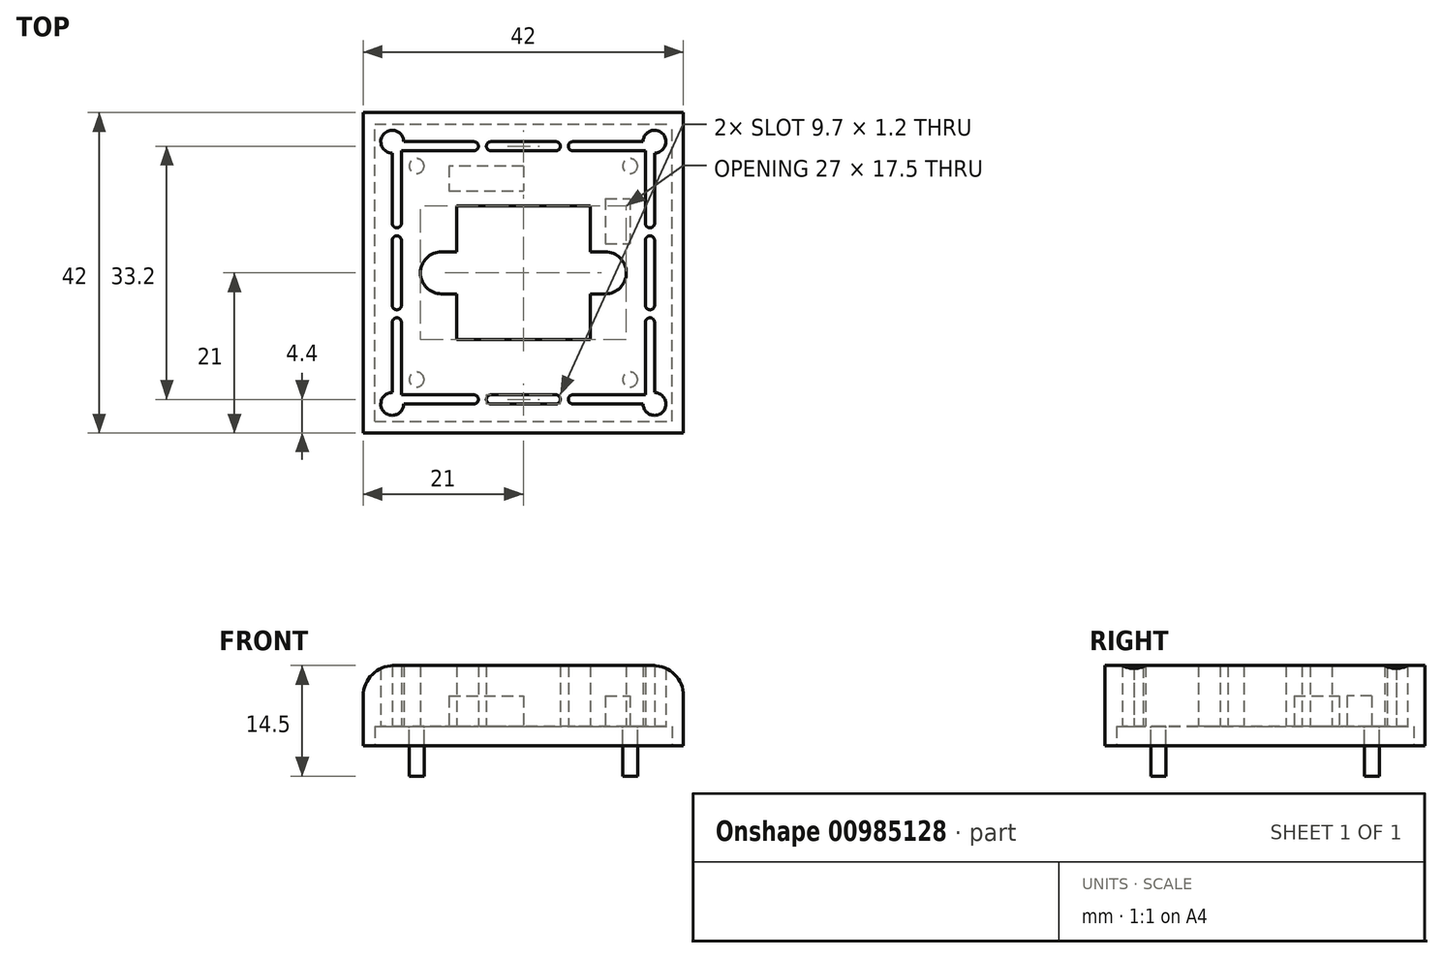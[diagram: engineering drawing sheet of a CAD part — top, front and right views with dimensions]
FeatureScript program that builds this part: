
annotation { "Feature Type Name" : "Feature", "Feature Type Description" : "" }
export const myFeature = defineFeature(function(context is Context, id is Id, definition is map)
    precondition{}
    {
        {
            var Q0;
            Q0=qCreatedBy(makeId("Top.planeOp"),FACE);
            var sketch = newSketch(context, id + "F0", { "sketchPlane" : qUnion([Q0])});
            skLineSegment(sketch, "E0.bottom", {"start": v(19, 19) * mm, "end": v(-19, 19) * mm, "construction": true});
            skLineSegment(sketch, "E0.top", {"start": v(19, -19) * mm, "end": v(-19, -19) * mm, "construction": true});
            skLineSegment(sketch, "E0.left", {"start": v(19, 19) * mm, "end": v(19, -19) * mm, "construction": true});
            skLineSegment(sketch, "E0.right", {"start": v(-19, 19) * mm, "end": v(-19, -19) * mm, "construction": true});
            skPoint(sketch, "E0.middle", {"position": v(0, 0) * mm});
            skPoint(sketch, "E1", {"position": v(19, 0) * mm});
            skPoint(sketch, "E2", {"position": v(-19, 0) * mm});
            skPoint(sketch, "E3", {"position": v(0, 19) * mm});
            skPoint(sketch, "E4", {"position": v(0, -19) * mm});
            skPoint(sketch, "E5", {"position": v(17.2, 0) * mm});
            skPoint(sketch, "E6", {"position": v(-17.2, 0) * mm});
            skLineSegment(sketch, "E7", {"start": v(-19, 0) * mm, "end": v(-17.2, 0) * mm, "construction": true});
            skLineSegment(sketch, "E8", {"start": v(19, 0) * mm, "end": v(17.2, 0) * mm, "construction": true});
            skLineSegment(sketch, "E9", {"start": v(0, 19) * mm, "end": v(0, 17.2) * mm, "construction": true});
            skLineSegment(sketch, "E10", {"start": v(0, -17.2) * mm, "end": v(0, -19) * mm, "construction": true});
            skPoint(sketch, "E11", {"position": v(-16, 16) * mm});
            skPoint(sketch, "E12", {"position": v(16, -16) * mm});
            skPoint(sketch, "E13", {"position": v(16, 16) * mm});
            skPoint(sketch, "E14", {"position": v(-16, -16) * mm});
            skPoint(sketch, "E15", {"position": v(17.2, 4.25) * mm});
            skPoint(sketch, "E16", {"position": v(17.2, -4.25) * mm});
            skPoint(sketch, "E17", {"position": v(16, -4.25) * mm});
            skPoint(sketch, "E18", {"position": v(16, 4.25) * mm});
            skPoint(sketch, "E19", {"position": v(-17.2, 4.25) * mm});
            skPoint(sketch, "E20", {"position": v(-16, 4.25) * mm});
            skPoint(sketch, "E21", {"position": v(-17.2, -4.25) * mm});
            skPoint(sketch, "E22", {"position": v(-16, -4.25) * mm});
            skPoint(sketch, "E23", {"position": v(-4.25, 17.2) * mm});
            skPoint(sketch, "E24", {"position": v(-4.25, 16) * mm});
            skPoint(sketch, "E25", {"position": v(4.25, 17.2) * mm});
            skPoint(sketch, "E26", {"position": v(4.25, 16) * mm});
            skPoint(sketch, "E27", {"position": v(-4.25, -16) * mm});
            skPoint(sketch, "E28", {"position": v(4.25, -16) * mm});
            skPoint(sketch, "E29", {"position": v(-4.25, -17.2) * mm});
            skPoint(sketch, "E30", {"position": v(4.25, -17.2) * mm});
            skLineSegment(sketch, "E31", {"start": v(17.2, 4.25) * mm, "end": v(17.2, -4.25) * mm});
            skLineSegment(sketch, "E32", {"start": v(16, 4.25) * mm, "end": v(16, -4.25) * mm});
            skLineSegment(sketch, "E33", {"start": v(4.25, 16) * mm, "end": v(-4.25, 16) * mm});
            skLineSegment(sketch, "E34", {"start": v(-4.25, 17.2) * mm, "end": v(4.25, 17.2) * mm});
            skLineSegment(sketch, "E35", {"start": v(-16, 4.25) * mm, "end": v(-16, -4.25) * mm});
            skLineSegment(sketch, "E36", {"start": v(-17.2, -4.25) * mm, "end": v(-17.2, 4.25) * mm});
            skLineSegment(sketch, "E37", {"start": v(-4.25, -16) * mm, "end": v(4.25, -16) * mm});
            skLineSegment(sketch, "E38", {"start": v(4.25, -17.2) * mm, "end": v(-4.25, -17.2) * mm});
            skArc(sketch, "E39", {"start": v(16, 4.25) * mm, "mid": v(16.6, 4.85) * mm, "end": v(17.2, 4.25) * mm});
            skArc(sketch, "E40", {"start": v(17.2, -4.25) * mm, "mid": v(16.6, -4.85) * mm, "end": v(16, -4.25) * mm});
            skArc(sketch, "E41", {"start": v(4.25, -16) * mm, "mid": v(4.85, -16.6) * mm, "end": v(4.25, -17.2) * mm});
            skArc(sketch, "E42", {"start": v(-4.25, -16) * mm, "mid": v(-4.85, -16.6) * mm, "end": v(-4.25, -17.2) * mm});
            skArc(sketch, "E43", {"start": v(-17.2, -4.25) * mm, "mid": v(-16.6, -4.85) * mm, "end": v(-16, -4.25) * mm});
            skArc(sketch, "E44", {"start": v(-17.2, 4.25) * mm, "mid": v(-16.6, 4.85) * mm, "end": v(-16, 4.25) * mm});
            skArc(sketch, "E45", {"start": v(-4.25, 16) * mm, "mid": v(-4.85, 16.6) * mm, "end": v(-4.25, 17.2) * mm});
            skArc(sketch, "E46", {"start": v(4.25, 16) * mm, "mid": v(4.85, 16.6) * mm, "end": v(4.25, 17.2) * mm});
            skPoint(sketch, "E47", {"position": v(-6.5, 16) * mm});
            skPoint(sketch, "E48", {"position": v(-6.5, 17.2) * mm});
            skPoint(sketch, "E49", {"position": v(-16, 6.5) * mm});
            skPoint(sketch, "E50", {"position": v(-17.2, 6.5) * mm});
            skPoint(sketch, "E51", {"position": v(6.5, 16) * mm});
            skPoint(sketch, "E52", {"position": v(6.5, 17.2) * mm});
            skPoint(sketch, "E53", {"position": v(16, 6.5) * mm});
            skPoint(sketch, "E54", {"position": v(17.2, 6.5) * mm});
            skPoint(sketch, "E55", {"position": v(-17.2, -6.5) * mm});
            skPoint(sketch, "E56", {"position": v(-16, -6.5) * mm});
            skPoint(sketch, "E57", {"position": v(17.2, -6.5) * mm});
            skPoint(sketch, "E58", {"position": v(16, -6.5) * mm});
            skPoint(sketch, "E59", {"position": v(6.5, -17.2) * mm});
            skPoint(sketch, "E60", {"position": v(6.5, -16) * mm});
            skPoint(sketch, "E61", {"position": v(-6.5, -17.2) * mm});
            skPoint(sketch, "E62", {"position": v(-6.5, -16) * mm});
            skLineSegment(sketch, "E63", {"start": v(-6.5, 17.2) * mm, "end": v(-6.5, 16) * mm, "construction": true});
            skLineSegment(sketch, "E64", {"start": v(-17.2, 6.5) * mm, "end": v(-16, 6.5) * mm, "construction": true});
            skLineSegment(sketch, "E65", {"start": v(6.5, 17.2) * mm, "end": v(6.5, 16) * mm, "construction": true});
            skLineSegment(sketch, "E66", {"start": v(16, 6.5) * mm, "end": v(17.2, 6.5) * mm, "construction": true});
            skLineSegment(sketch, "E67", {"start": v(-17.2, -6.5) * mm, "end": v(-16, -6.5) * mm, "construction": true});
            skLineSegment(sketch, "E68", {"start": v(-6.5, -16) * mm, "end": v(-6.5, -17.2) * mm, "construction": true});
            skLineSegment(sketch, "E69", {"start": v(16, -6.5) * mm, "end": v(17.2, -6.5) * mm, "construction": true});
            skLineSegment(sketch, "E70", {"start": v(6.5, -16) * mm, "end": v(6.5, -17.2) * mm, "construction": true});
            skArc(sketch, "E71", {"start": v(-6.5, 17.2) * mm, "mid": v(-5.9, 16.6) * mm, "end": v(-6.5, 16) * mm});
            skArc(sketch, "E72", {"start": v(-16, 6.5) * mm, "mid": v(-16.6, 5.9) * mm, "end": v(-17.2, 6.5) * mm});
            skArc(sketch, "E73", {"start": v(6.5, 17.2) * mm, "mid": v(5.9, 16.6) * mm, "end": v(6.5, 16) * mm});
            skArc(sketch, "E74", {"start": v(17.2, 6.5) * mm, "mid": v(16.6, 5.9) * mm, "end": v(16, 6.5) * mm});
            skArc(sketch, "E75", {"start": v(-16, -6.5) * mm, "mid": v(-16.6, -5.9) * mm, "end": v(-17.2, -6.5) * mm});
            skArc(sketch, "E76", {"start": v(-6.5, -16) * mm, "mid": v(-5.9, -16.6) * mm, "end": v(-6.5, -17.2) * mm});
            skArc(sketch, "E77", {"start": v(6.5, -16) * mm, "mid": v(5.9, -16.6) * mm, "end": v(6.5, -17.2) * mm});
            skArc(sketch, "E78", {"start": v(17.2, -6.5) * mm, "mid": v(16.6, -5.9) * mm, "end": v(16, -6.5) * mm});
            skLineSegment(sketch, "E79", {"start": v(6.5, 17.2) * mm, "end": v(16, 17.2) * mm});
            skLineSegment(sketch, "E80", {"start": v(6.5, 16) * mm, "end": v(16, 16) * mm});
            skLineSegment(sketch, "E81", {"start": v(16, 6.5) * mm, "end": v(16, 16) * mm});
            skLineSegment(sketch, "E82", {"start": v(17.2, 16) * mm, "end": v(17.2, 6.5) * mm});
            skLineSegment(sketch, "E83", {"start": v(-16, 17.2) * mm, "end": v(-6.5, 17.2) * mm});
            skLineSegment(sketch, "E84", {"start": v(-16, 16) * mm, "end": v(-6.5, 16) * mm});
            skLineSegment(sketch, "E85", {"start": v(-16, 16) * mm, "end": v(-16, 6.5) * mm});
            skLineSegment(sketch, "E86", {"start": v(-17.2, 6.5) * mm, "end": v(-17.2, 16) * mm});
            skLineSegment(sketch, "E87", {"start": v(-16, -6.5) * mm, "end": v(-16, -16) * mm});
            skLineSegment(sketch, "E88", {"start": v(-6.5, -16) * mm, "end": v(-16, -16) * mm});
            skLineSegment(sketch, "E89", {"start": v(-17.2, -6.5) * mm, "end": v(-17.2, -16) * mm});
            skLineSegment(sketch, "E90", {"start": v(-16, -17.2) * mm, "end": v(-6.5, -17.2) * mm});
            skLineSegment(sketch, "E91", {"start": v(6.5, -17.2) * mm, "end": v(16, -17.2) * mm});
            skLineSegment(sketch, "E92", {"start": v(6.5, -16) * mm, "end": v(16, -16) * mm});
            skLineSegment(sketch, "E93", {"start": v(17.2, -16) * mm, "end": v(17.2, -6.5) * mm});
            skLineSegment(sketch, "E94", {"start": v(16, -6.5) * mm, "end": v(16, -16) * mm});
            skLineSegment(sketch, "E95", {"start": v(-17.2, 6.5) * mm, "end": v(-19, 6.5) * mm, "construction": true});
            skLineSegment(sketch, "E96", {"start": v(-17.2, -6.5) * mm, "end": v(-19, -6.5) * mm, "construction": true});
            skLineSegment(sketch, "E97", {"start": v(-6.5, 17.2) * mm, "end": v(-6.5, 19) * mm, "construction": true});
            skLineSegment(sketch, "E98", {"start": v(-6.5, -17.2) * mm, "end": v(-6.5, -19) * mm, "construction": true});
            skLineSegment(sketch, "E99", {"start": v(6.5, -17.2) * mm, "end": v(6.5, -19) * mm, "construction": true});
            skLineSegment(sketch, "E100", {"start": v(17.2, -6.5) * mm, "end": v(19, -6.5) * mm, "construction": true});
            skLineSegment(sketch, "E101", {"start": v(17.2, 6.5) * mm, "end": v(19, 6.5) * mm, "construction": true});
            skLineSegment(sketch, "E102", {"start": v(6.5, 17.2) * mm, "end": v(6.5, 19) * mm, "construction": true});
            skPoint(sketch, "E103", {"position": v(-11.25, 17.2) * mm});
            skPoint(sketch, "E104", {"position": v(-11.25, 16) * mm});
            skPoint(sketch, "E105", {"position": v(-17.2, 11.25) * mm});
            skPoint(sketch, "E106", {"position": v(-16, 11.25) * mm});
            skPoint(sketch, "E107", {"position": v(11.25, 17.2) * mm});
            skPoint(sketch, "E108", {"position": v(11.25, 16) * mm});
            skPoint(sketch, "E109", {"position": v(16, 11.25) * mm});
            skPoint(sketch, "E110", {"position": v(17.2, 11.25) * mm});
            skPoint(sketch, "E111", {"position": v(16, -11.25) * mm});
            skPoint(sketch, "E112", {"position": v(17.2, -11.25) * mm});
            skPoint(sketch, "E113", {"position": v(11.25, -16) * mm});
            skPoint(sketch, "E114", {"position": v(11.25, -17.2) * mm});
            skPoint(sketch, "E115", {"position": v(-11.25, -16) * mm});
            skPoint(sketch, "E116", {"position": v(-11.25, -17.2) * mm});
            skPoint(sketch, "E117", {"position": v(-16, -11.25) * mm});
            skPoint(sketch, "E118", {"position": v(-17.2, -11.25) * mm});
            skLineSegment(sketch, "E119", {"start": v(-17.2, 11.25) * mm, "end": v(-16, 11.25) * mm, "construction": true});
            skLineSegment(sketch, "E120", {"start": v(-11.25, 17.2) * mm, "end": v(-11.25, 16) * mm, "construction": true});
            skLineSegment(sketch, "E121", {"start": v(-11.25, -16) * mm, "end": v(-11.25, -17.2) * mm, "construction": true});
            skLineSegment(sketch, "E122", {"start": v(-16, -11.25) * mm, "end": v(-17.2, -11.25) * mm, "construction": true});
            skLineSegment(sketch, "E123", {"start": v(11.25, 17.2) * mm, "end": v(11.25, 16) * mm, "construction": true});
            skLineSegment(sketch, "E124", {"start": v(16, 11.25) * mm, "end": v(17.2, 11.25) * mm, "construction": true});
            skLineSegment(sketch, "E125", {"start": v(11.25, -17.2) * mm, "end": v(11.25, -16) * mm, "construction": true});
            skLineSegment(sketch, "E126", {"start": v(16, -11.25) * mm, "end": v(17.2, -11.25) * mm, "construction": true});
            skPoint(sketch, "E127", {"position": v(-14, 14) * mm});
            skLineSegment(sketch, "E128", {"start": v(-14, 19) * mm, "end": v(-14, 14) * mm, "construction": true});
            skLineSegment(sketch, "E129", {"start": v(-14, 14) * mm, "end": v(-19, 14) * mm, "construction": true});
            skPoint(sketch, "E130", {"position": v(-14, -14) * mm});
            skLineSegment(sketch, "E131", {"start": v(-19, -14) * mm, "end": v(-14, -14) * mm, "construction": true});
            skLineSegment(sketch, "E132", {"start": v(-14, -19) * mm, "end": v(-14, -14) * mm, "construction": true});
            skPoint(sketch, "E133", {"position": v(14, -14) * mm});
            skLineSegment(sketch, "E134", {"start": v(14, -19) * mm, "end": v(14, -14) * mm, "construction": true});
            skLineSegment(sketch, "E135", {"start": v(14, -14) * mm, "end": v(19, -14) * mm, "construction": true});
            skPoint(sketch, "E136", {"position": v(14, 14) * mm});
            skLineSegment(sketch, "E137", {"start": v(14, 19) * mm, "end": v(14, 14) * mm, "construction": true});
            skLineSegment(sketch, "E138", {"start": v(19, 14) * mm, "end": v(14, 14) * mm, "construction": true});
            skPoint(sketch, "E139", {"position": v(16, 0) * mm});
            skPoint(sketch, "E140", {"position": v(0, 16) * mm});
            skPoint(sketch, "E141", {"position": v(-16, 0) * mm});
            skPoint(sketch, "E142", {"position": v(0, -16) * mm});
            skLineSegment(sketch, "E143", {"start": v(16, 0) * mm, "end": v(17.2, 0) * mm, "construction": true});
            skLineSegment(sketch, "E144", {"start": v(0, 17.2) * mm, "end": v(0, 16) * mm, "construction": true});
            skLineSegment(sketch, "E145", {"start": v(0, -16) * mm, "end": v(0, -17.2) * mm, "construction": true});
            skLineSegment(sketch, "E146", {"start": v(-17.2, 0) * mm, "end": v(-16, 0) * mm, "construction": true});
            skPoint(sketch, "E147", {"position": v(-17.2, 17.2) * mm});
            skPoint(sketch, "E148", {"position": v(17.2, 17.2) * mm});
            skPoint(sketch, "E149", {"position": v(-17.2, -17.2) * mm});
            skPoint(sketch, "E150", {"position": v(17.2, -17.2) * mm});
            skLineSegment(sketch, "E151", {"start": v(16, 4.25) * mm, "end": v(17.2, 4.25) * mm, "construction": true});
            skLineSegment(sketch, "E152", {"start": v(16, -4.25) * mm, "end": v(17.2, -4.25) * mm, "construction": true});
            skLineSegment(sketch, "E153", {"start": v(-4.25, 16) * mm, "end": v(-4.25, 17.2) * mm, "construction": true});
            skLineSegment(sketch, "E154", {"start": v(4.25, 16) * mm, "end": v(4.25, 17.2) * mm, "construction": true});
            skLineSegment(sketch, "E155", {"start": v(-16, 4.25) * mm, "end": v(-17.2, 4.25) * mm, "construction": true});
            skLineSegment(sketch, "E156", {"start": v(-16, -4.25) * mm, "end": v(-17.2, -4.25) * mm, "construction": true});
            skLineSegment(sketch, "E157", {"start": v(-4.25, -16) * mm, "end": v(-4.25, -17.2) * mm, "construction": true});
            skLineSegment(sketch, "E158", {"start": v(4.25, -16) * mm, "end": v(4.25, -17.2) * mm, "construction": true});
            skLineSegment(sketch, "E159", {"start": v(-6.5, 17.2) * mm, "end": v(-4.25, 17.2) * mm, "construction": true});
            skLineSegment(sketch, "E160", {"start": v(4.25, 17.2) * mm, "end": v(6.5, 17.2) * mm, "construction": true});
            skLineSegment(sketch, "E161", {"start": v(17.2, 6.5) * mm, "end": v(17.2, 4.25) * mm, "construction": true});
            skLineSegment(sketch, "E162", {"start": v(17.2, -6.5) * mm, "end": v(17.2, -4.25) * mm, "construction": true});
            skLineSegment(sketch, "E163", {"start": v(6.5, -17.2) * mm, "end": v(4.25, -17.2) * mm, "construction": true});
            skLineSegment(sketch, "E164", {"start": v(-4.25, -17.2) * mm, "end": v(-6.5, -17.2) * mm, "construction": true});
            skLineSegment(sketch, "E165", {"start": v(-17.2, -6.5) * mm, "end": v(-17.2, -4.25) * mm, "construction": true});
            skLineSegment(sketch, "E166", {"start": v(-17.2, 4.25) * mm, "end": v(-17.2, 6.5) * mm, "construction": true});
            skCircle(sketch, "E167", {"center": v(14, 14) * mm, "radius": 0.97 * mm});
            skPoint(sketch, "E168", {"position": v(14, 14.97) * mm});
            skPoint(sketch, "E169", {"position": v(14.97, 14) * mm});
            skPoint(sketch, "E170", {"position": v(16, 14) * mm});
            skPoint(sketch, "E171", {"position": v(14, 16) * mm});
            skCircle(sketch, "E172", {"center": v(-14, 14) * mm, "radius": 0.97 * mm});
            skPoint(sketch, "E173", {"position": v(-14, 14.97) * mm});
            skPoint(sketch, "E174", {"position": v(-14.97, 14) * mm});
            skCircle(sketch, "E175", {"center": v(-14, -14) * mm, "radius": 0.97 * mm});
            skCircle(sketch, "E176", {"center": v(14, -14) * mm, "radius": 0.97 * mm});
            skPoint(sketch, "E177", {"position": v(14, -14.97) * mm});
            skPoint(sketch, "E178", {"position": v(14.97, -14) * mm});
            skPoint(sketch, "E179", {"position": v(-14.97, -14) * mm});
            skPoint(sketch, "E180", {"position": v(-14, -14.97) * mm});
            skLineSegment(sketch, "E181.bottom", {"start": v(8.75, 8.75) * mm, "end": v(-8.75, 8.75) * mm});
            skLineSegment(sketch, "E181.top", {"start": v(8.75, -8.75) * mm, "end": v(-8.75, -8.75) * mm});
            skLineSegment(sketch, "E181.left", {"start": v(8.75, 8.75) * mm, "end": v(8.75, 2.75) * mm});
            skLineSegment(sketch, "E181.right", {"start": v(-8.75, 8.75) * mm, "end": v(-8.75, 2.75) * mm});
            skLineSegment(sketch, "E182.bottom", {"start": v(-21, 21) * mm, "end": v(-2.62, 21) * mm});
            skLineSegment(sketch, "E182.top", {"start": v(-21, -21) * mm, "end": v(-2.63, -21) * mm});
            skLineSegment(sketch, "E182.left", {"start": v(-21, 21) * mm, "end": v(-21, -21) * mm});
            skLineSegment(sketch, "E182.right", {"start": v(21, 21) * mm, "end": v(21, -21) * mm});
            skPoint(sketch, "E183", {"position": v(0, 21) * mm});
            skPoint(sketch, "E184", {"position": v(-2.62, 21) * mm});
            skPoint(sketch, "E185", {"position": v(2.62, 21) * mm});
            skLineSegment(sketch, "E186.trimOffspring", {"start": v(2.62, 21) * mm, "end": v(21, 21) * mm});
            skPoint(sketch, "E187", {"position": v(0, -21) * mm});
            skPoint(sketch, "E188", {"position": v(-2.63, -21) * mm});
            skPoint(sketch, "E189", {"position": v(2.63, -21) * mm});
            skLineSegment(sketch, "E190.trimOffspring", {"start": v(2.63, -21) * mm, "end": v(21, -21) * mm});
            skLineSegment(sketch, "E191", {"start": v(-2.62, 21) * mm, "end": v(2.63, 21) * mm});
            skLineSegment(sketch, "E192", {"start": v(-2.63, -21) * mm, "end": v(2.63, -21) * mm});
            skPoint(sketch, "E193", {"position": v(-8.75, 0) * mm});
            skPoint(sketch, "E194", {"position": v(8.75, 0) * mm});
            skPoint(sketch, "E195", {"position": v(8.75, -2.75) * mm});
            skPoint(sketch, "E196", {"position": v(8.75, 2.75) * mm});
            skPoint(sketch, "E197", {"position": v(-8.75, -2.75) * mm});
            skPoint(sketch, "E198", {"position": v(-8.75, 2.75) * mm});
            skLineSegment(sketch, "E199", {"start": v(-8.75, -2.75) * mm, "end": v(8.75, -2.75) * mm, "construction": true});
            skLineSegment(sketch, "E200", {"start": v(8.75, 2.75) * mm, "end": v(-8.75, 2.75) * mm, "construction": true});
            skPoint(sketch, "E201", {"position": v(10.75, 0) * mm});
            skPoint(sketch, "E202", {"position": v(-10.75, 0) * mm});
            skLineSegment(sketch, "E203", {"start": v(10.75, 0) * mm, "end": v(8.75, 0) * mm, "construction": true});
            skLineSegment(sketch, "E204", {"start": v(-10.75, 0) * mm, "end": v(-8.75, 0) * mm, "construction": true});
            skLineSegment(sketch, "E205", {"start": v(-8.75, -2.75) * mm, "end": v(-10.75, -2.75) * mm});
            skLineSegment(sketch, "E206", {"start": v(-8.75, 2.75) * mm, "end": v(-10.75, 2.75) * mm});
            skLineSegment(sketch, "E207", {"start": v(8.75, -2.75) * mm, "end": v(10.75, -2.75) * mm});
            skLineSegment(sketch, "E208", {"start": v(8.75, 2.75) * mm, "end": v(10.75, 2.75) * mm});
            skArc(sketch, "E209", {"start": v(-10.75, 2.75) * mm, "mid": v(-13.5, 0) * mm, "end": v(-10.75, -2.75) * mm});
            skArc(sketch, "E210", {"start": v(10.75, -2.75) * mm, "mid": v(13.5, 0) * mm, "end": v(10.75, 2.75) * mm});
            skLineSegment(sketch, "E211.trimOffspring", {"start": v(-8.75, -2.75) * mm, "end": v(-8.75, -8.75) * mm});
            skLineSegment(sketch, "E212.trimOffspring", {"start": v(8.75, -2.75) * mm, "end": v(8.75, -8.75) * mm});
            skLineSegment(sketch, "E213", {"start": v(-16, -6.5) * mm, "end": v(-16, -4.25) * mm});
            skLineSegment(sketch, "E214", {"start": v(-16, 4.25) * mm, "end": v(-16, 6.5) * mm});
            skLineSegment(sketch, "E215", {"start": v(-6.5, -16) * mm, "end": v(-4.25, -16) * mm});
            skLineSegment(sketch, "E216", {"start": v(4.25, -16) * mm, "end": v(6.5, -16) * mm});
            skLineSegment(sketch, "E217", {"start": v(16, -4.25) * mm, "end": v(16, -6.5) * mm});
            skLineSegment(sketch, "E218", {"start": v(16, 4.25) * mm, "end": v(16, 6.5) * mm});
            skLineSegment(sketch, "E219", {"start": v(6.5, 16) * mm, "end": v(4.25, 16) * mm});
            skLineSegment(sketch, "E220", {"start": v(-4.25, 16) * mm, "end": v(-6.5, 16) * mm});
            skArc(sketch, "E221", {"start": v(-15.7, 17.2) * mm, "mid": v(-18.26, 18.26) * mm, "end": v(-17.2, 15.7) * mm});
            skLineSegment(sketch, "E222", {"start": v(-17.2, 16) * mm, "end": v(-17.2, 17.2) * mm, "construction": true});
            skLineSegment(sketch, "E223", {"start": v(-17.2, 17.2) * mm, "end": v(-17.2, 19) * mm, "construction": true});
            skLineSegment(sketch, "E224", {"start": v(-16, 17.2) * mm, "end": v(-17.2, 17.2) * mm, "construction": true});
            skLineSegment(sketch, "E225", {"start": v(-17.2, 17.2) * mm, "end": v(-19, 17.2) * mm, "construction": true});
            skArc(sketch, "E226", {"start": v(17.2, 15.7) * mm, "mid": v(18.26, 18.26) * mm, "end": v(15.7, 17.2) * mm});
            skLineSegment(sketch, "E227", {"start": v(16, 17.2) * mm, "end": v(17.2, 17.2) * mm, "construction": true});
            skLineSegment(sketch, "E228", {"start": v(17.2, 16) * mm, "end": v(17.2, 17.2) * mm, "construction": true});
            skLineSegment(sketch, "E229", {"start": v(17.2, 17.2) * mm, "end": v(17.2, 19) * mm, "construction": true});
            skLineSegment(sketch, "E230", {"start": v(17.2, 17.2) * mm, "end": v(19, 17.2) * mm, "construction": true});
            skArc(sketch, "E231", {"start": v(-17.2, -15.7) * mm, "mid": v(-18.26, -18.26) * mm, "end": v(-15.7, -17.2) * mm});
            skArc(sketch, "E232", {"start": v(15.7, -17.2) * mm, "mid": v(18.26, -18.26) * mm, "end": v(17.2, -15.7) * mm});
            skLineSegment(sketch, "E233", {"start": v(17.2, -16) * mm, "end": v(17.2, -17.2) * mm, "construction": true});
            skLineSegment(sketch, "E234", {"start": v(17.2, -17.2) * mm, "end": v(17.2, -19) * mm, "construction": true});
            skLineSegment(sketch, "E235", {"start": v(16, -17.2) * mm, "end": v(17.2, -17.2) * mm, "construction": true});
            skLineSegment(sketch, "E236", {"start": v(17.2, -17.2) * mm, "end": v(19, -17.2) * mm, "construction": true});
            skLineSegment(sketch, "E237", {"start": v(-17.2, -16) * mm, "end": v(-17.2, -17.2) * mm, "construction": true});
            skLineSegment(sketch, "E238", {"start": v(-17.2, -17.2) * mm, "end": v(-17.2, -19) * mm, "construction": true});
            skLineSegment(sketch, "E239", {"start": v(-16, -17.2) * mm, "end": v(-17.2, -17.2) * mm, "construction": true});
            skLineSegment(sketch, "E240", {"start": v(-17.2, -17.2) * mm, "end": v(-19, -17.2) * mm, "construction": true});
            skPoint(sketch, "E241", {"position": v(15.7, 17.2) * mm});
            skPoint(sketch, "E242", {"position": v(17.2, 15.7) * mm});
            skPoint(sketch, "E243", {"position": v(-17.2, 15.7) * mm});
            skPoint(sketch, "E244", {"position": v(-15.7, 17.2) * mm});
            skPoint(sketch, "E245", {"position": v(-17.2, -15.7) * mm});
            skPoint(sketch, "E246", {"position": v(-15.7, -17.2) * mm});
            skPoint(sketch, "E247", {"position": v(15.7, -17.2) * mm});
            skPoint(sketch, "E248", {"position": v(17.2, -15.7) * mm});
            skLineSegment(sketch, "E249.bottom", {"start": v(-19.5, -19.5) * mm, "end": v(19.5, -19.5) * mm});
            skLineSegment(sketch, "E249.top", {"start": v(-19.5, 19.5) * mm, "end": v(19.5, 19.5) * mm});
            skLineSegment(sketch, "E249.left", {"start": v(-19.5, -19.5) * mm, "end": v(-19.5, 19.5) * mm});
            skLineSegment(sketch, "E249.right", {"start": v(19.5, -19.5) * mm, "end": v(19.5, 19.5) * mm});
            skPoint(sketch, "E250", {"position": v(-8.75, 10.75) * mm});
            skPoint(sketch, "E251", {"position": v(-8.75, 14) * mm});
            skPoint(sketch, "E252", {"position": v(0, 8.75) * mm});
            skPoint(sketch, "E253", {"position": v(0, 10.75) * mm});
            skPoint(sketch, "E254", {"position": v(0, 14) * mm});
            skLineSegment(sketch, "E255", {"start": v(0, 14) * mm, "end": v(0, 10.75) * mm});
            skLineSegment(sketch, "E256", {"start": v(-8.75, 10.75) * mm, "end": v(0, 10.75) * mm});
            skLineSegment(sketch, "E257", {"start": v(0, 14) * mm, "end": v(-8.75, 14) * mm});
            skLineSegment(sketch, "E258", {"start": v(-8.75, 14) * mm, "end": v(-9.75, 14) * mm});
            skLineSegment(sketch, "E259", {"start": v(-9.75, 14) * mm, "end": v(-9.75, 10.75) * mm});
            skLineSegment(sketch, "E260", {"start": v(-9.75, 10.75) * mm, "end": v(-8.75, 10.75) * mm});
            skPoint(sketch, "E261", {"position": v(10.75, 8.75) * mm});
            skPoint(sketch, "E262", {"position": v(14, 8.75) * mm});
            skLineSegment(sketch, "E263", {"start": v(10.75, 8.75) * mm, "end": v(10.75, 3.81) * mm});
            skLineSegment(sketch, "E264", {"start": v(10.75, 3.81) * mm, "end": v(14, 3.81) * mm});
            skLineSegment(sketch, "E265", {"start": v(14, 3.81) * mm, "end": v(14, 8.75) * mm});
            skLineSegment(sketch, "E266", {"start": v(10.75, 8.75) * mm, "end": v(10.75, 9.75) * mm});
            skLineSegment(sketch, "E267", {"start": v(10.75, 9.75) * mm, "end": v(14, 9.75) * mm});
            skLineSegment(sketch, "E268", {"start": v(14, 9.75) * mm, "end": v(14, 8.75) * mm});
            skSolve(sketch);
        }
        {
            var Q0;
            Q0=qSketchRegion(id+"F0",true);
            var Q1;
            Q1=makeQuery(id+"F0.imprint","IMPRINT",FACE,{"disambiguationData":[TD([[makeQuery(id+"F0.imprint","IMPRINT",EDGE,{"derivedFrom":sQuery(id+"F0.wireOp",EDGE,"E176")}),1.0]])]});
            var Q2;
            Q2=makeQuery(id+"F0.imprint","IMPRINT",FACE,{"disambiguationData":[TD([[makeQuery(id+"F0.imprint","IMPRINT",EDGE,{"derivedFrom":sQuery(id+"F0.wireOp",EDGE,"E175")}),1.0]])]});
            var Q3;
            Q3=makeQuery(id+"F0.imprint","IMPRINT",FACE,{"disambiguationData":[TD([[makeQuery(id+"F0.imprint","IMPRINT",EDGE,{"derivedFrom":sQuery(id+"F0.wireOp",EDGE,"E172")}),1.0]])]});
            var Q4;
            Q4=makeQuery(id+"F0.imprint","IMPRINT",FACE,{"disambiguationData":[TD([[makeQuery(id+"F0.imprint","IMPRINT",EDGE,{"derivedFrom":sQuery(id+"F0.wireOp",EDGE,"E167")}),1.0]])]});
            var Q5;
            Q5=makeQuery(id+"F0.imprint","IMPRINT",FACE,{"disambiguationData":[TD([[makeQuery(id+"F0.imprint","IMPRINT",EDGE,{"derivedFrom":sQuery(id+"F0.wireOp",EDGE,"E32")}),-1.0]])]});
            var Q6;
            Q6=makeQuery(id+"F0.imprint","IMPRINT",FACE,{"disambiguationData":[TD([[makeQuery(id+"F0.imprint","IMPRINT",EDGE,{"derivedFrom":sQuery(id+"F0.wireOp",EDGE,"E31")}),1.0]])]});
            var Q7;
            Q7=makeQuery(id+"F0.imprint","IMPRINT",FACE,{"disambiguationData":[TD([[makeQuery(id+"F0.imprint","IMPRINT",EDGE,{"derivedFrom":sQuery(id+"F0.wireOp",EDGE,"E263")}),1.0]])]});
            var Q8;
            Q8=makeQuery(id+"F0.imprint","IMPRINT",FACE,{"disambiguationData":[TD([[makeQuery(id+"F0.imprint","IMPRINT",EDGE,{"derivedFrom":sQuery(id+"F0.wireOp",EDGE,"E255")}),-1.0]])]});
            extrude(context, id + "F1", {"entities" : qUnion([Q0, Q1, Q2, Q3, Q4, Q5, Q6, Q7, Q8]), "depth" : 9 * mm, "offsetDistance" : 25 * mm});
        }
        {
            var Q0;
            Q0=makeQuery(id+"F1.opExtrude","CAP_EDGE",EDGE,{"disambiguationData":[OSD([sQuery(id+"F0.wireOp",EDGE,"E182.left")])],"isStart":false});
            var Q1;
            Q1=makeQuery(id+"F1.opExtrude","CAP_EDGE",EDGE,{"disambiguationData":[OSD([sQuery(id+"F0.wireOp",EDGE,"E182.right")])],"isStart":false});
            fillet(context, id + "F2", {"entities" : qUnion([Q0, Q1]), "radius" : 4 * mm, "tangentPropagation" : true, "allowEdgeOverflow" : false});
        }
        {
            var Q0;
            Q0=makeQuery(id+"F0.imprint","IMPRINT",FACE,{"disambiguationData":[TD([[makeQuery(id+"F0.imprint","IMPRINT",EDGE,{"derivedFrom":sQuery(id+"F0.wireOp",EDGE,"E175")}),1.0]])]});
            var Q1;
            Q1=makeQuery(id+"F0.imprint","IMPRINT",FACE,{"disambiguationData":[TD([[makeQuery(id+"F0.imprint","IMPRINT",EDGE,{"derivedFrom":sQuery(id+"F0.wireOp",EDGE,"E176")}),1.0]])]});
            var Q2;
            Q2=makeQuery(id+"F0.imprint","IMPRINT",FACE,{"disambiguationData":[TD([[makeQuery(id+"F0.imprint","IMPRINT",EDGE,{"derivedFrom":sQuery(id+"F0.wireOp",EDGE,"E172")}),1.0]])]});
            var Q3;
            Q3=makeQuery(id+"F0.imprint","IMPRINT",FACE,{"disambiguationData":[TD([[makeQuery(id+"F0.imprint","IMPRINT",EDGE,{"derivedFrom":sQuery(id+"F0.wireOp",EDGE,"E167")}),1.0]])]});
            var Q4;
            Q4=sQuery(id+"F0.wireOp",EDGE,"E175");
            var Q5;
            Q5=sQuery(id+"F0.wireOp",EDGE,"E176");
            var Q6;
            Q6=sQuery(id+"F0.wireOp",EDGE,"E167");
            var Q7;
            Q7=sQuery(id+"F0.wireOp",EDGE,"E172");
            extrude(context, id + "F3", {"entities" : qUnion([Q0, Q1, Q2, Q3]), "operationType" : NewBodyOperationType.ADD, "surfaceEntities" : qUnion([Q4, Q5, Q6, Q7]), "oppositeDirection" : true, "depth" : 5.5 * mm, "offsetDistance" : 25 * mm});
        }
        {
            var Q0;
            Q0=makeQuery(id+"F0.imprint","IMPRINT",FACE,{"disambiguationData":[TD([[makeQuery(id+"F0.imprint","IMPRINT",EDGE,{"derivedFrom":sQuery(id+"F0.wireOp",EDGE,"E31")}),1.0]])]});
            extrude(context, id + "F4", {"entities" : qUnion([Q0]), "operationType" : NewBodyOperationType.ADD, "oppositeDirection" : true, "depth" : 1.5 * mm, "offsetDistance" : 25 * mm});
        }
        {
            var Q0;
            Q0=makeQuery(id+"F4.opExtrude","CAP_FACE",FACE,{"disambiguationData":[OSD([sQuery(id+"F0.wireOp",EDGE,"E31"),sQuery(id+"F0.wireOp",EDGE,"E34"),sQuery(id+"F0.wireOp",EDGE,"E36"),sQuery(id+"F0.wireOp",EDGE,"E38"),sQuery(id+"F0.wireOp",EDGE,"E39"),sQuery(id+"F0.wireOp",EDGE,"E40"),sQuery(id+"F0.wireOp",EDGE,"E41"),sQuery(id+"F0.wireOp",EDGE,"E42"),sQuery(id+"F0.wireOp",EDGE,"E43"),sQuery(id+"F0.wireOp",EDGE,"E44"),sQuery(id+"F0.wireOp",EDGE,"E45"),sQuery(id+"F0.wireOp",EDGE,"E46"),sQuery(id+"F0.wireOp",EDGE,"E71"),sQuery(id+"F0.wireOp",EDGE,"E72"),sQuery(id+"F0.wireOp",EDGE,"E73"),sQuery(id+"F0.wireOp",EDGE,"E74"),sQuery(id+"F0.wireOp",EDGE,"E75"),sQuery(id+"F0.wireOp",EDGE,"E76"),sQuery(id+"F0.wireOp",EDGE,"E77"),sQuery(id+"F0.wireOp",EDGE,"E78"),sQuery(id+"F0.wireOp",EDGE,"E79"),sQuery(id+"F0.wireOp",EDGE,"E82"),sQuery(id+"F0.wireOp",EDGE,"E83"),sQuery(id+"F0.wireOp",EDGE,"E86"),sQuery(id+"F0.wireOp",EDGE,"E89"),sQuery(id+"F0.wireOp",EDGE,"E90"),sQuery(id+"F0.wireOp",EDGE,"E91"),sQuery(id+"F0.wireOp",EDGE,"E93"),sQuery(id+"F0.wireOp",EDGE,"E213"),sQuery(id+"F0.wireOp",EDGE,"E214"),sQuery(id+"F0.wireOp",EDGE,"E215"),sQuery(id+"F0.wireOp",EDGE,"E216"),sQuery(id+"F0.wireOp",EDGE,"E217"),sQuery(id+"F0.wireOp",EDGE,"E218"),sQuery(id+"F0.wireOp",EDGE,"E219"),sQuery(id+"F0.wireOp",EDGE,"E220"),sQuery(id+"F0.wireOp",EDGE,"E221"),sQuery(id+"F0.wireOp",EDGE,"E226"),sQuery(id+"F0.wireOp",EDGE,"E231"),sQuery(id+"F0.wireOp",EDGE,"E232"),sQuery(id+"F0.wireOp",EDGE,"E249.bottom"),sQuery(id+"F0.wireOp",EDGE,"E249.top"),sQuery(id+"F0.wireOp",EDGE,"E249.left"),sQuery(id+"F0.wireOp",EDGE,"E249.right")])],"isStart":false});
            extrude(context, id + "F5", {"entities" : qUnion([Q0]), "operationType" : NewBodyOperationType.REMOVE, "oppositeDirection" : true, "depth" : 2.5 * mm, "offsetDistance" : 25 * mm});
        }
        {
            var Q0;
            Q0=makeQuery(id+"F0.imprint","IMPRINT",FACE,{"disambiguationData":[TD([[makeQuery(id+"F0.imprint","IMPRINT",EDGE,{"derivedFrom":sQuery(id+"F0.wireOp",EDGE,"E182.bottom")}),-1.0]])]});
            extrude(context, id + "F6", {"entities" : qUnion([Q0]), "operationType" : NewBodyOperationType.ADD, "oppositeDirection" : true, "depth" : 1.5 * mm, "offsetDistance" : 25 * mm});
        }
        {
            var Q0;
            Q0=makeQuery(id+"F0.imprint","IMPRINT",FACE,{"disambiguationData":[TD([[makeQuery(id+"F0.imprint","IMPRINT",EDGE,{"derivedFrom":sQuery(id+"F0.wireOp",EDGE,"E263")}),1.0]])]});
            var Q1;
            Q1=makeQuery(id+"F0.imprint","IMPRINT",FACE,{"disambiguationData":[TD([[makeQuery(id+"F0.imprint","IMPRINT",EDGE,{"derivedFrom":sQuery(id+"F0.wireOp",EDGE,"E255")}),-1.0]])]});
            extrude(context, id + "F7", {"entities" : qUnion([Q0, Q1]), "operationType" : NewBodyOperationType.REMOVE, "depth" : 5 * mm, "offsetDistance" : 25 * mm});
        }
        {
            var Q0;
            Q0=makeQuery(id+"F0.imprint","IMPRINT",FACE,{"disambiguationData":[TD([[makeQuery(id+"F0.imprint","IMPRINT",EDGE,{"derivedFrom":sQuery(id+"F0.wireOp",EDGE,"E32")}),-1.0]])]});
            extrude(context, id + "F8", {"entities" : qUnion([Q0]), "operationType" : NewBodyOperationType.REMOVE, "depth" : 1 * mm, "offsetDistance" : 25 * mm});
        }
    });
